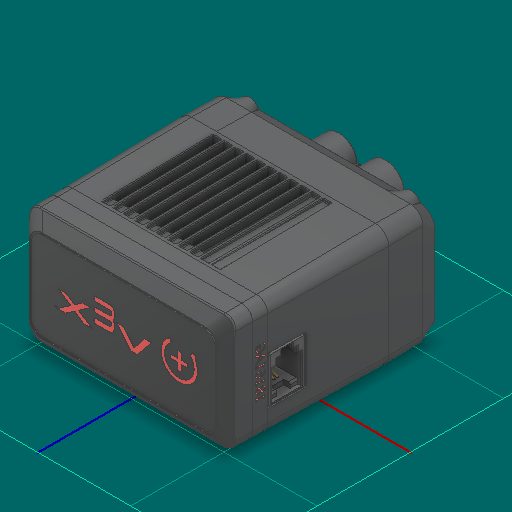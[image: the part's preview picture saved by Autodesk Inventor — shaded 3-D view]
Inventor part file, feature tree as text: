
AUTODESK INVENTOR PART (.ipt)
format: ipt  version: 2025 (Build 290162000, 162)  size: 13,124,096 bytes
history: native  units: in
note: dims shown in document units (in); Inventor stores cm internally (conversion verified against a paired STEP export)
features: other x19, sketch x2
ambient origin geometry x8: Origin, YZ Plane, XZ Plane, XY Plane, X Axis, Y Axis, Z Axis, Center Point
bodies: Solid1 (feature_tree), Solid2 (feature_tree), Solid7 (feature_tree), Solid8 (feature_tree), Solid9 (feature_tree), Solid20 (feature_tree), Solid21 (feature_tree), Solid22 (feature_tree)
feature tree (21):
  other  "V5 Motor.ipt"
  other  "Solid1::V5 Motor.ipt"
  other  "Solid2::V5 Motor.ipt"
  other  "Solid4::V5 Motor.ipt"
  other  "Solid6::V5 Motor.ipt"
  other  "Solid7::V5 Motor.ipt"
  other  "Solid8::V5 Motor.ipt"
  other  "Solid9::V5 Motor.ipt"
  other  "Solid14::V5 Motor.ipt"
  other  "Solid16::V5 Motor.ipt"
  other  "Solid17::V5 Motor.ipt"
  other  "Solid18::V5 Motor.ipt"
  other  "Solid19::V5 Motor.ipt"
  other  "Solid20::V5 Motor.ipt"
  other  "Solid21::V5 Motor.ipt"
  other  "Solid22::V5 Motor.ipt"
  other  "TaggingFeature1"
  sketch  "Sketch1"  dims[d0=0.3937in]
  sketch  "Sketch2"  dims[d4=0.0in d5=0.0in]
  other  "iInsert:1"
  other  "iInsert:2"
